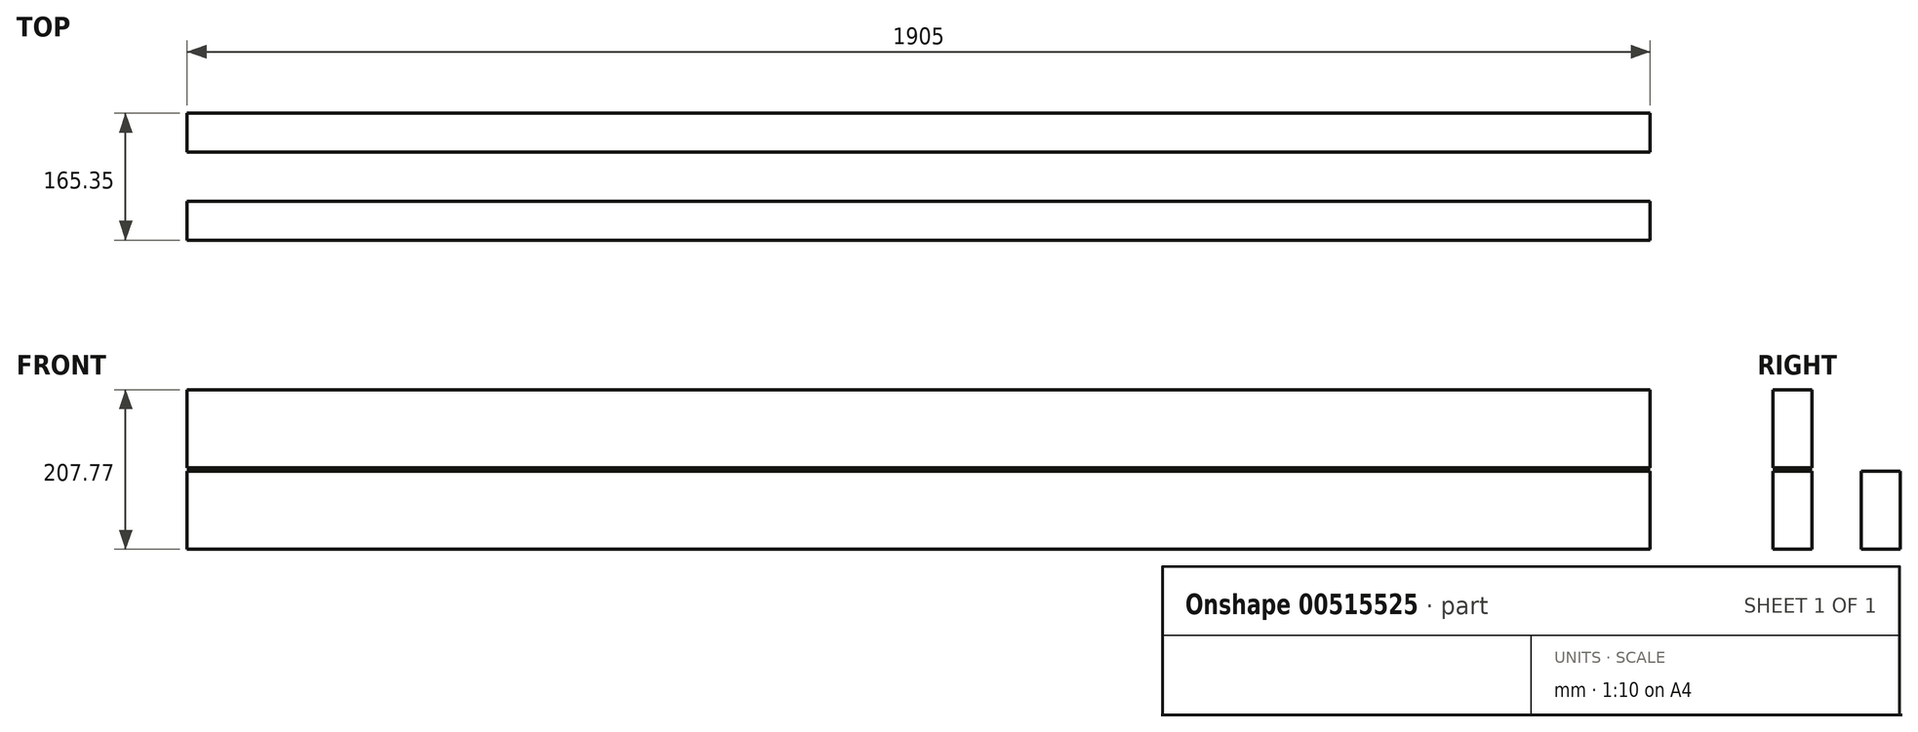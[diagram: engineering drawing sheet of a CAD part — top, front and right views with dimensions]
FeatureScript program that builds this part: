
annotation { "Feature Type Name" : "Feature", "Feature Type Description" : "" }
export const myFeature = defineFeature(function(context is Context, id is Id, definition is map)
    precondition{}
    {
        {
            var Q0;
            Q0=qCreatedBy(makeId("Right.planeOp"),FACE);
            var sketch = newSketch(context, id + "F0", { "sketchPlane" : qUnion([Q0])});
            skLineSegment(sketch, "E0.bottom", {"start": v(25.4, -50.8) * mm, "end": v(-25.4, -50.8) * mm});
            skLineSegment(sketch, "E0.top", {"start": v(25.4, 50.8) * mm, "end": v(-25.4, 50.8) * mm});
            skLineSegment(sketch, "E0.left", {"start": v(25.4, -50.8) * mm, "end": v(25.4, 50.8) * mm});
            skLineSegment(sketch, "E0.right", {"start": v(-25.4, -50.8) * mm, "end": v(-25.4, 50.8) * mm});
            skPoint(sketch, "E0.middle", {"position": v(0, 0) * mm});
            skSolve(sketch);
        }
        {
            var Q0;
            Q0 = qSketchRegion(id + "F0", true);
            extrude(context, id + "F1", {"entities" : qUnion([Q0]), "oppositeDirection" : true, "depth" : 1905 * mm, "offsetDistance" : 25.4 * mm});
        }
        {
            var Q0;
            Q0=makeQuery(id+"F1.opExtrude","SWEPT_BODY",BODY,{"disambiguationData":[OSD([sQuery(id+"F0.wireOp",EDGE,"E0.bottom"),sQuery(id+"F0.wireOp",EDGE,"E0.top"),sQuery(id+"F0.wireOp",EDGE,"E0.left"),sQuery(id+"F0.wireOp",EDGE,"E0.right")])]});
            transform(context, id + "F2", {"entities" : qUnion([Q0]), "transformType" : TransformType.TRANSLATION_3D, "dx" : 0 * mm, "dy" : 0 * mm, "dz" : 106.17 * mm, "makeCopy" : true});
        }
        {
            var Q0;
            Q0=makeQuery(id+"F1.opExtrude","SWEPT_BODY",BODY,{"disambiguationData":[OSD([sQuery(id+"F0.wireOp",EDGE,"E0.bottom"),sQuery(id+"F0.wireOp",EDGE,"E0.top"),sQuery(id+"F0.wireOp",EDGE,"E0.left"),sQuery(id+"F0.wireOp",EDGE,"E0.right")])]});
            transform(context, id + "F3", {"entities" : qUnion([Q0]), "transformType" : TransformType.TRANSLATION_3D, "dx" : 0 * mm, "dy" : 114.55 * mm, "dz" : 0 * mm, "makeCopy" : true});
        }
    });
